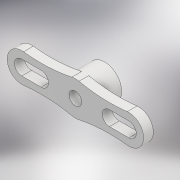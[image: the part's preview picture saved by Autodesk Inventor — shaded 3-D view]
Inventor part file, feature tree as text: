
AUTODESK INVENTOR PART (.ipt)
format: ipt  version: 2018.2 (Build 222227000, 227)  size: 160,256 bytes
history: native  units: mm
features: extrude x3, plane x1, sketch x1
ambient origin geometry x8: Origin, YZ Plane, XZ Plane, XY Plane, X Axis, Y Axis, Z Axis, Center Point
bodies: Solid1 (feature_tree)
feature tree (5):
  extrude  "Extrusion1"  Depth=7.0mm
  extrude  "Extrusion2"  Depth=3.0mm
  extrude  "Extrusion3"  Depth=2.0mm TaperAngle=0.0deg
  plane  "Work Plane1"
  sketch  "Sketch2"  dims[d0=2.62mm d1=7.0mm d6=3.0mm d7=2.0mm d8=0.0mm d9=4.0mm d10=0.0mm d11=3.0mm d12=6.0mm d13=0.0mm d14=30.0mm d15=3.0mm d16=4.0mm d17=7.0mm]
